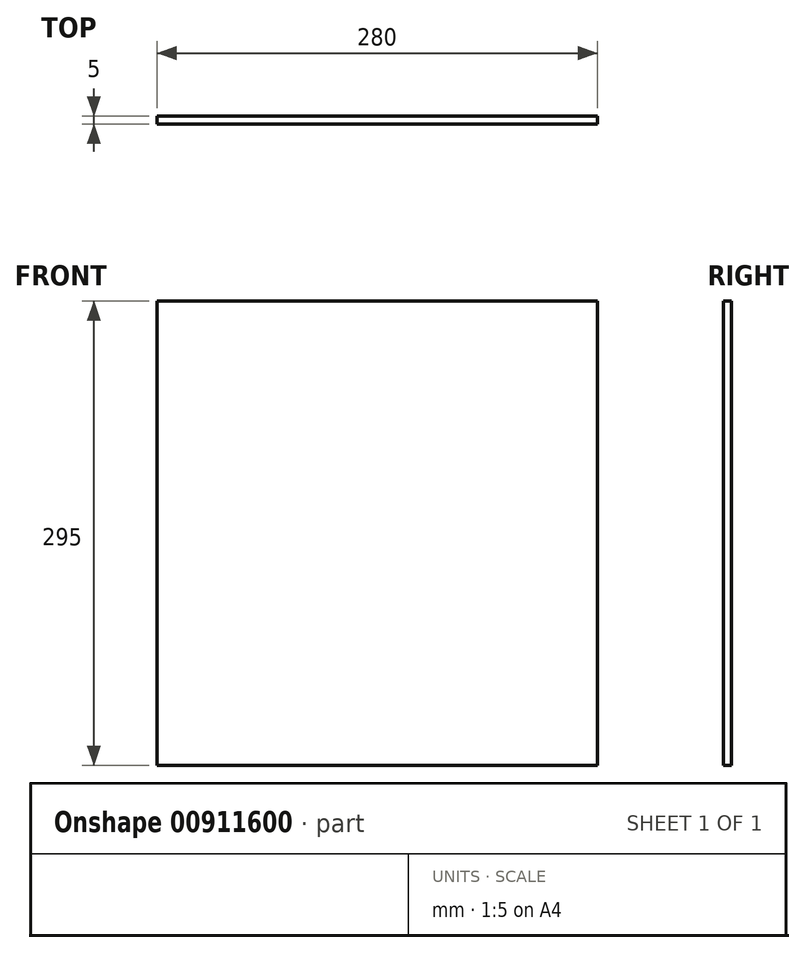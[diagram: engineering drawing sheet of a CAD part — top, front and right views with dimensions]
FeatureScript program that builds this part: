
annotation { "Feature Type Name" : "Feature", "Feature Type Description" : "" }
export const myFeature = defineFeature(function(context is Context, id is Id, definition is map)
    precondition{}
    {
        {
            var Q0;
            Q0=qCreatedBy(makeId("Front.planeOp"),FACE);
            var sketch = newSketch(context, id + "F0", { "sketchPlane" : qUnion([Q0])});
            skLineSegment(sketch, "E0.bottom", {"start": v(0, 0) * mm, "end": v(280, 0) * mm});
            skLineSegment(sketch, "E0.top", {"start": v(0, 295) * mm, "end": v(280, 295) * mm});
            skLineSegment(sketch, "E0.left", {"start": v(0, 0) * mm, "end": v(0, 295) * mm});
            skLineSegment(sketch, "E0.right", {"start": v(280, 0) * mm, "end": v(280, 295) * mm});
            skSolve(sketch);
        }
        {
            var Q0;
            Q0 = qSketchRegion(id + "F0", true);
            extrude(context, id + "F1", {"entities" : qUnion([Q0]), "depth" : 5 * mm, "offsetDistance" : 25 * mm});
        }
    });
